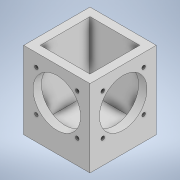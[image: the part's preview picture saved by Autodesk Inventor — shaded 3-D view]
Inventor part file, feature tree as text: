
AUTODESK INVENTOR PART (.ipt)
format: ipt  version: 2021 (Build 250183000, 183)  size: 148,480 bytes
history: native  units: mm
features: sketch x7, extrude x4, hole x3
ambient origin geometry x8: Origin, YZ Plane, XZ Plane, XY Plane, X Axis, Y Axis, Z Axis, Center Point
bodies: Solid1 (feature_tree)
feature tree (14):
  extrude  "Extrusion1"  Depth=60.0mm
  extrude  "Extrusion2"  Depth=45.0mm
  extrude  "Extrusion3"  Depth=60.0mm TaperAngle=0.0deg
  extrude  "Extrusion4"  Depth=15.0mm TaperAngle=0.0deg
  hole  "Hole1"  [1 undecoded]
  hole  "Hole2"  [1 undecoded]
  hole  "Hole3"  [1 undecoded]
  sketch  "Sketch1"  dims[d0=60.0mm d1=60.0mm]
  sketch  "Sketch2"  dims[d2=70.0mm d3=0.0mm d4=45.0mm]
  sketch  "Sketch3"  dims[d5=45.0mm d6=60.0mm d7=0.0mm]
  sketch  "Sketch4"  dims[d8=43.0mm d9=15.0mm d10=0.0mm]
  sketch  "Sketch5"  dims[d11=43.0mm d12=15.0mm d13=0.0mm]
  sketch  "Sketch7"  dims[d14=3.302mm d15=6.0mm d16=7.938mm d17=4.166mm d18=90.0deg d19=8.0mm d20=0.0mm d21=37.0mm]
  sketch  "Sketch8"  dims[d22=37.0mm d23=3.302mm d24=5.0mm d25=7.938mm d26=4.166mm d27=90.0deg d28=6.0mm d29=0.0mm d30=37.0mm d31=37.0mm d32=3.302mm d33=5.0mm d34=7.938mm d35=4.166mm d36=90.0deg d37=6.0mm d38=0.0mm]
note: 3 required parameter values undecoded (feature->parameter linkage not recoverable at this tier; creation-order binding heuristic only, values carry confidence <= 0.55)
